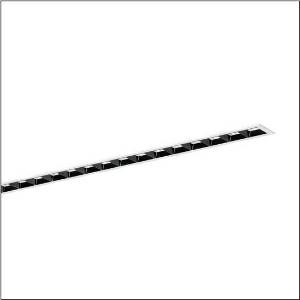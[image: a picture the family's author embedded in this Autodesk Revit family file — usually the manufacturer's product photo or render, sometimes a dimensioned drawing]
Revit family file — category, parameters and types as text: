
# Revit family: silica_r__21_51mx12tat4w_4f36
name_source: partatom
category: Lighting Fixtures
units: mm (PartAtom-declared; Revit-internal decimal feet)

## family parameters
Cut with Voids When Loaded = No
Host = Face
Light Source = No
Part Type = Normal
Room Calculation Point = No
Round Connector Dimension = Use Diameter
Shared = No

## types (1)
- --- (1 x LED, 3720 lm, 32.1 W, 6500K)
    Apparent Load = 32 VA
    CIE Flux Codes = 84 100 100 100 100
    Color Rendering = 80
    Color Temperature = 6500K
    Default Elevation = 1800 mm
    Description = Silica® 21, office luminaire, primary light control with darklight reflector, of PMMA, black, CAT 2 (L<= 3000cd/m²), light emission: direct distribution, primary light characteristic: symmetric, installation type: recessed, LED, rated luminous flux: 3.720lm, luminous efficacy: 110lm/W, light colour: 8tw, colour temperature: 2700..6500K, control gear: DALI DT8, with terminal, 3+2-pole, max. 2.5mm², mains connection: 220..240V, AC, 50/60Hz, rated input power: 33.8W, luminaire housing, of aluminium, traffic white (RAL 9016), length: 1.228mm, width: 79mm, height: 53mm, protection rating (complete): IP20, insulation class (complete): insulation class I (protective earthing), certification: CE, ENEC, VDE, permissible operating ambient temperature: 0..+35°C, standard: EN 50419, packaging unit: 1 piece
    Height = 0 mm  [stored 0 ft]
    Lamp = 1 x LED
    Lamp Light Flux = 3720 lm
    Lamp Power = 32.1 W
    Lamp count = 1
    Length = 1227 mm
    Luminous efficacy = 116 lm/W
    Manufacturer = Siteco
    ModVariant = No
    Model = 51MX12TAT4W
    Mounting Place = Ceiling
    Mounting Type = Recessed
    Number of Poles = 1
    OnlyDefault = Yes
    Power Factor = 1
    Product Name = Silica® 21
    Product group = office luminaire | ceiling recessed
    ProductGroupID = 401
    Protection Class = Protection class I
    Protection Degree = IP 20
    RLX_Detail_Level = 1
    RLX_Emergency_Light_Flux = 0 lm
    RLX_Emergency_Type = 0
    RLX_Emergency_Type_DB = No
    RlxData = <blob elided: 35369 chars, md5=2dc4e4e8>
    Socket = socket
    Standby Power = 0 W
    System Light Flux = 3720 lm
    System Power = 32 W
    Type Comments = individual setting
    Type Image = l_1335880.jpg
    URL = http://relux.com
    VarID = @adj_140178
    Voltage = 0 V
    Weight = 0.00 kg
    Width = 79 mm

note: [stored X ft] marks values corroborated as IEEE doubles in the binary element streams (Revit-internal decimal feet)

## geometry (parser evidence)
native form markers: Blend x4, Sweep x9
no freeform markers — native parametric forms only
